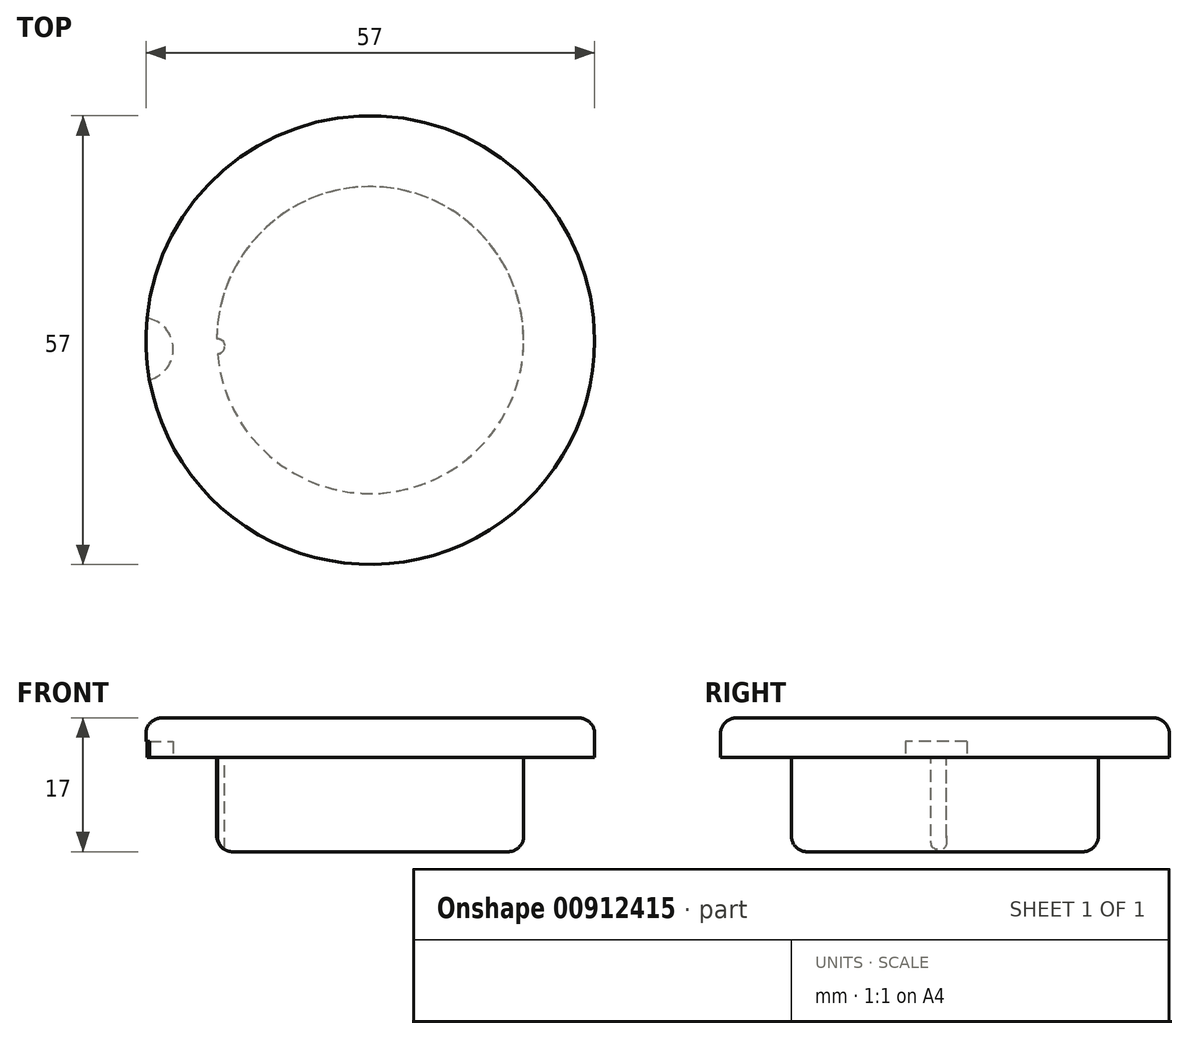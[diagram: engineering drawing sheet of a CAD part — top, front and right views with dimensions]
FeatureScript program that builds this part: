
annotation { "Feature Type Name" : "Feature", "Feature Type Description" : "" }
export const myFeature = defineFeature(function(context is Context, id is Id, definition is map)
    precondition{}
    {
        {
            var Q0;
            Q0=qCreatedBy(makeId("Top.planeOp"),FACE);
            var sketch = newSketch(context, id + "F0", { "sketchPlane" : qUnion([Q0])});
            skCircle(sketch, "E0", {"center": v(0, 0) * mm, "radius": 28.5 * mm});
            skCircle(sketch, "E1", {"center": v(0, 0) * mm, "radius": 19.5 * mm});
            skCircle(sketch, "E2", {"center": v(-19.48, -0.8) * mm, "radius": 1 * mm});
            skArc(sketch, "E3", {"start": v(-28.05, -5.03) * mm, "mid": v(-25.02, -0.99) * mm, "end": v(-28.36, 2.8) * mm});
            skSolve(sketch);
        }
        {
            var Q0;
            Q0=makeQuery(id+"F0.imprint","IMPRINT",FACE,{"disambiguationData":[TD([[makeQuery(id+"F0.imprint","IMPRINT",EDGE,{"derivedFrom":sQuery(id+"F0.wireOp",EDGE,"E0")}),1.0]])]});
            var Q1;
            {var subQ0=sQuery(id+"F0.wireOp",EDGE,"E2");var subQ1=sQuery(id+"F0.wireOp",EDGE,"E1");var subQ2=makeQuery(id+"F0.imprint","INTERSECT",VERTEX,{"disambiguationData":[OD(0.0)],"derivedFrom":[subQ1,subQ0]});Q1=makeQuery(id+"F0.imprint","IMPRINT",FACE,{"disambiguationData":[TD([[makeQuery(id+"F0.imprint","IMPRINT",EDGE,{"disambiguationData":[TD([[subQ2,1.0]])],"derivedFrom":subQ1}),-1.0]])]});}
            var Q2;
            {var subQ0=sQuery(id+"F0.wireOp",EDGE,"E3");Q2=makeQuery(id+"F0.imprint","IMPRINT",FACE,{"disambiguationData":[TD([[makeQuery(id+"F0.imprint","IMPRINT",EDGE,{"derivedFrom":subQ0}),-1.0]])]});}
            extrude(context, id + "F1", {"entities" : qUnion([Q0, Q1, Q2]), "depth" : 5 * mm, "offsetDistance" : 25 * mm});
        }
        {
            var Q0;
            Q0=makeQuery(id+"F0.imprint","IMPRINT",FACE,{"disambiguationData":[TD([[makeQuery(id+"F0.imprint","IMPRINT",EDGE,{"derivedFrom":sQuery(id+"F0.wireOp",EDGE,"E1")}),1.0]])]});
            extrude(context, id + "F2", {"entities" : qUnion([Q0]), "operationType" : NewBodyOperationType.ADD, "depth" : 5 * mm, "offsetDistance" : 25 * mm});
        }
        {
            var Q0;
            {var subQ0=sQuery(id+"F0.wireOp",EDGE,"E2");var subQ1=sQuery(id+"F0.wireOp",EDGE,"E1");var subQ2=makeQuery(id+"F0.imprint","INTERSECT",VERTEX,{"disambiguationData":[OD(0.0)],"derivedFrom":[subQ1,subQ0]});Q0=makeQuery(id+"F0.imprint","IMPRINT",FACE,{"disambiguationData":[TD([[makeQuery(id+"F0.imprint","IMPRINT",EDGE,{"disambiguationData":[TD([[subQ2,-1.0]])],"derivedFrom":subQ1}),1.0]])]});}
            extrude(context, id + "F3", {"entities" : qUnion([Q0]), "operationType" : NewBodyOperationType.ADD, "oppositeDirection" : true, "depth" : 12 * mm, "offsetDistance" : 25 * mm});
        }
        {
            var Q0;
            Q0=makeQuery(id+"F1.opExtrude","CAP_EDGE",EDGE,{"disambiguationData":[OSD([sQuery(id+"F0.wireOp",EDGE,"E0")])],"isStart":false});
            fillet(context, id + "F4", {"entities" : qUnion([Q0]), "radius" : 2 * mm, "tangentPropagation" : true, "allowEdgeOverflow" : false});
        }
        {
            var Q0;
            Q0=makeQuery(id+"F3.opExtrude","CAP_EDGE",EDGE,{"disambiguationData":[OSD([sQuery(id+"F0.wireOp",EDGE,"E1")])],"isStart":false});
            fillet(context, id + "F5", {"entities" : qUnion([Q0]), "radius" : 2 * mm, "tangentPropagation" : true, "allowEdgeOverflow" : false});
        }
        {
            var Q0;
            {var subQ0=sQuery(id+"F0.wireOp",EDGE,"E3");Q0=makeQuery(id+"F0.imprint","IMPRINT",FACE,{"disambiguationData":[TD([[makeQuery(id+"F0.imprint","IMPRINT",EDGE,{"derivedFrom":subQ0}),1.0]])]});}
            extrude(context, id + "F6", {"entities" : qUnion([Q0]), "operationType" : NewBodyOperationType.REMOVE, "depth" : 2 * mm, "offsetDistance" : 25 * mm});
        }
    });
